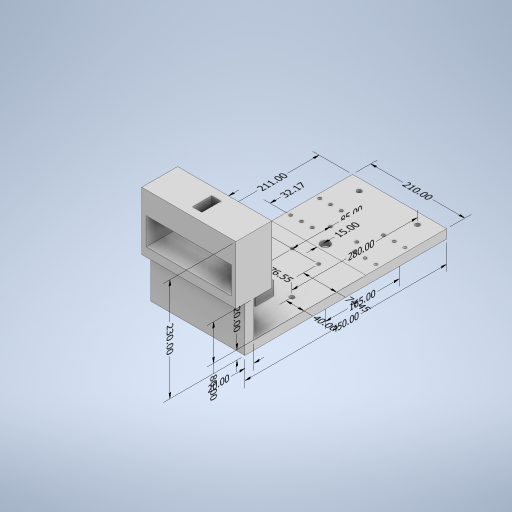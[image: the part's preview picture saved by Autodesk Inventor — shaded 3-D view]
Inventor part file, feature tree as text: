
AUTODESK INVENTOR PART (.ipt)
format: ipt  version: 2023 (Build 270158000, 158)  size: 448,512 bytes
history: native  units: mm
features: other x19, sketch x13, extrude x12, split x1
ambient origin geometry x8: Origin, YZ Plane, XZ Plane, XY Plane, X Axis, Y Axis, Z Axis, Center Point
bodies: Body1 (feature_tree)
feature tree (45):
  other  "Sólido1"
  other  "Anotaciones"
  extrude  "Extrusión1"  Depth=450.0mm
  extrude  "Extrusión2"  Depth=20.0mm
  extrude  "Extrusión3"  Depth=20.0mm
  extrude  "Extrusión4"  Depth=60.0mm
  extrude  "Extrusión5"  Depth=190.0mm
  extrude  "Extrusión6"  Depth=60.0mm TaperAngle=0.0deg
  extrude  "Extrusión7"  Depth=43.0mm
  extrude  "Extrusión8"  Depth=10.0mm
  extrude  "Extrusión9"  Depth=10.0mm
  extrude  "Extrusión10"  Depth=10.0mm
  extrude  "Extrusión11"  Depth=25.0mm
  extrude  "Extrusión12"  Depth=40.0mm
  split  "Dividir1"
  sketch  "Boceto1"  dims[d0=20.0mm d1=450.0mm]
  sketch  "Boceto2"  dims[d2=210.0mm d3=0.0mm d4=20.0mm]
  sketch  "Boceto3"  dims[d5=80.0mm d6=0.0mm d7=20.0mm]
  sketch  "Boceto4"  dims[d8=210.0mm d9=60.0mm]
  sketch  "Boceto5"  dims[d10=130.0mm d11=0.0mm d12=190.0mm]
  sketch  "Boceto6"  dims[d13=60.0mm d16=60.0mm d17=0.0mm]
  sketch  "Boceto7"  dims[d18=21.0mm d19=43.0mm]
  sketch  "Boceto8"  dims[d21=43.0mm d22=0.0mm d23=10.0mm]
  sketch  "Boceto9"  dims[d24=10.0mm d25=10.0mm]
  sketch  "Boceto10"  dims[d26=10.0mm d27=165.0mm]
  sketch  "Boceto11"  dims[d28=25.0mm d29=25.0mm]
  sketch  "Boceto12"  dims[d30=165.0mm d31=40.0mm]
  sketch  "Boceto13"  dims[d32=40.0mm d33=40.0mm d34=40.0mm d35=43.0mm d36=0.0mm d44=20.0mm d45=10.0mm d46=0.0mm d51=7.0mm d52=7.0mm d54=7.0mm d55=20.0mm d56=0.0mm d59=20.0mm d62=20.0mm d63=0.0mm d64=20.0mm d65=30.0mm d66=30.0mm d68=74.0mm d69=31.0mm d70=84.0mm d71=41.0mm d72=10.0mm d73=0.0mm d74=84.0mm d75=41.0mm d76=30.0mm d77=0.0mm d78=7.0mm d79=68.0mm d80=80.0mm d81=7.6mm d82=10.0mm d83=7.0mm d84=30.0mm d85=0.0mm d103=180.0mm d110=180.0mm d100=9.422185mm d101=1.193524mm d102=20.0mm d104=9.135179mm d105=32.166555mm d106=5.22954mm d107=15.0mm d111=5.992022mm d112=3.930543mm d113=20.0mm d114=6.486022mm d115=31.0mm d116=1.81804mm d117=76.551816mm d118=1.179967mm d119=74.448184mm d120=85.0mm d121=5.107273mm d122=40.0mm d40=9.477646mm d41=4.784189mm d42=80.0mm d43=280.0mm d86=125.0mm d87=4.2098mm d88=450.0mm d89=0.666568mm d90=4.428063mm d91=230.0mm d92=6.47995mm d93=211.0mm d94=5.175864mm d95=6.811682mm d96=165.0mm d97=0.788992mm d98=0.638053mm d99=210.0mm]
  other  "Cota lineal 2"
  other  "Cota lineal 3"
  other  "Cota lineal 4"
  other  "Cota lineal 5"
  other  "Cota lineal 6"
  other  "Cota lineal 7"
  other  "Cota lineal 8"
  other  "Cota lineal 9"
  other  "Cota lineal 10"
  other  "Cota lineal 11"
  other  "Cota lineal 12"
  other  "Cota lineal 13"
  other  "Cota lineal 14"
  other  "Cota lineal 15"
  other  "Cota lineal 16"
  other  "Cota lineal 17"
  other  "Cota lineal 18"
